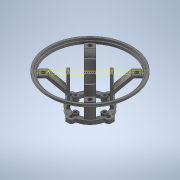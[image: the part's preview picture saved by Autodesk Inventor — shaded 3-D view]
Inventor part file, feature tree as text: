
AUTODESK INVENTOR PART (.ipt)
format: ipt  version: 2020 (Build 240168000, 168)  size: 771,072 bytes
history: native  units: mm
features: projected_geometry x29, sketch x17, extrude x11, other x6, pattern_circular x1, sweep x1, fillet x1
ambient origin geometry x8: Origin, YZ Plane, XZ Plane, XY Plane, X Axis, Y Axis, Z Axis, Center Point
bodies: Body1 (feature_tree)
feature tree (66):
  other  "Твердое тело1"
  sketch  "Эскиз1"
  extrude  "Выдавливание1"  Depth=44.0mm
  extrude  "Выдавливание2"  Depth=3.8mm
  sketch  "Эскиз3"
  extrude  "Выдавливание4"  Depth=40.0mm TaperAngle=360.0deg
  pattern_circular  "Круговой массив1"  [2 undecoded]
  other  "РабПлоскость2"
  sketch  "Эскиз5"
  other  "РабПлоскость1"
  sketch  "Эскиз6"
  sketch  "Эскиз7"
  extrude  "Выдавливание6"  Depth=4.5mm
  sketch  "Эскиз8"
  extrude  "Выдавливание7"  Depth=3.0mm
  sketch  "Эскиз9"
  other  "РабПлоскость3"
  sketch  "Эскиз10"
  sweep  "Сдвиг1"
  extrude  "Выдавливание8"  Depth=1.0mm
  extrude  "Выдавливание9"  TaperAngle=45.0deg  [1 undecoded]
  sketch  "Эскиз14"
  other  "РабПлоскость4"
  sketch  "Эскиз15"
  extrude  "Выдавливание10"  TaperAngle=135.0deg  [1 undecoded]
  extrude  "Выдавливание11"  Depth=34.0mm
  other  "РабПлоскость5"
  sketch  "Эскиз16"
  extrude  "Выдавливание13"  Depth=4.0mm TaperAngle=0.0deg
  extrude  "Выдавливание12"  Depth=3.0mm
  fillet  "Сопряжение1"  [1 undecoded]
  sketch  "Эскиз2"
  sketch  "Эскиз4"
  projected_geometry  "Спроецированная петля1"
  projected_geometry  "Спроецированная петля2"
  projected_geometry  "Спроецированная петля3"
  projected_geometry  "Спроецированная петля4"
  projected_geometry  "Спроецированная петля5"
  projected_geometry  "Спроецированная петля6"
  projected_geometry  "Спроецированная петля7"
  projected_geometry  "Спроецированная петля8"
  projected_geometry  "Спроецированная петля9"
  projected_geometry  "Спроецированная петля10"
  projected_geometry  "Спроецированная петля11"
  projected_geometry  "Спроецированная петля12"
  projected_geometry  "Спроецированная петля13"
  projected_geometry  "Спроецированная петля14"
  projected_geometry  "Спроецированная петля15"
  projected_geometry  "Спроецированная петля16"
  projected_geometry  "Спроецированная петля17"
  projected_geometry  "Спроецированная петля18"
  projected_geometry  "Спроецированная петля19"
  projected_geometry  "Спроецированная петля20"
  sketch  "Эскиз11"
  projected_geometry  "Спроецированная петля21"
  projected_geometry  "Спроецированная петля22"
  projected_geometry  "Спроецированная петля23"
  sketch  "3D эскиз1"
  sketch  "Эскиз12"
  sketch  "Эскиз13"
  projected_geometry  "Спроецированная петля24"
  projected_geometry  "Спроецированная петля25"
  projected_geometry  "Спроецированная петля26"
  projected_geometry  "Спроецированная петля27"
  projected_geometry  "Спроецированная петля28"
  projected_geometry  "Спроецированная петля29"
note: 5 required parameter values undecoded (feature->parameter linkage not recoverable at this tier; creation-order binding heuristic only, values carry confidence <= 0.55)
